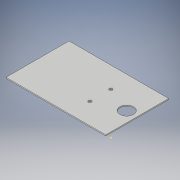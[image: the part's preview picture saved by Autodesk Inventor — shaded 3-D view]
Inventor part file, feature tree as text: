
AUTODESK INVENTOR PART (.ipt)
format: ipt  version: 2019 (Build 230136000, 136)  size: 103,936 bytes
history: native  units: mm
features: sketch x3, extrude x2
ambient origin geometry x8: Origin, YZ Plane, XZ Plane, XY Plane, X Axis, Y Axis, Z Axis, Center Point
bodies: Solid1 (feature_tree)
feature tree (5):
  extrude  "Extrusion1"  Depth=1.0mm TaperAngle=0.0deg
  sketch  "Sketch3"  dims[d1=60.0mm d2=1.0mm d3=0.0mm]
  sketch  "Sketch4"  dims[d9=3.0mm d10=3.0mm]
  extrude  "Extrusion3"  Depth=3.0mm
  sketch  "Sketch5"  dims[d11=13.0mm d12=1.0mm d13=0.0mm]
